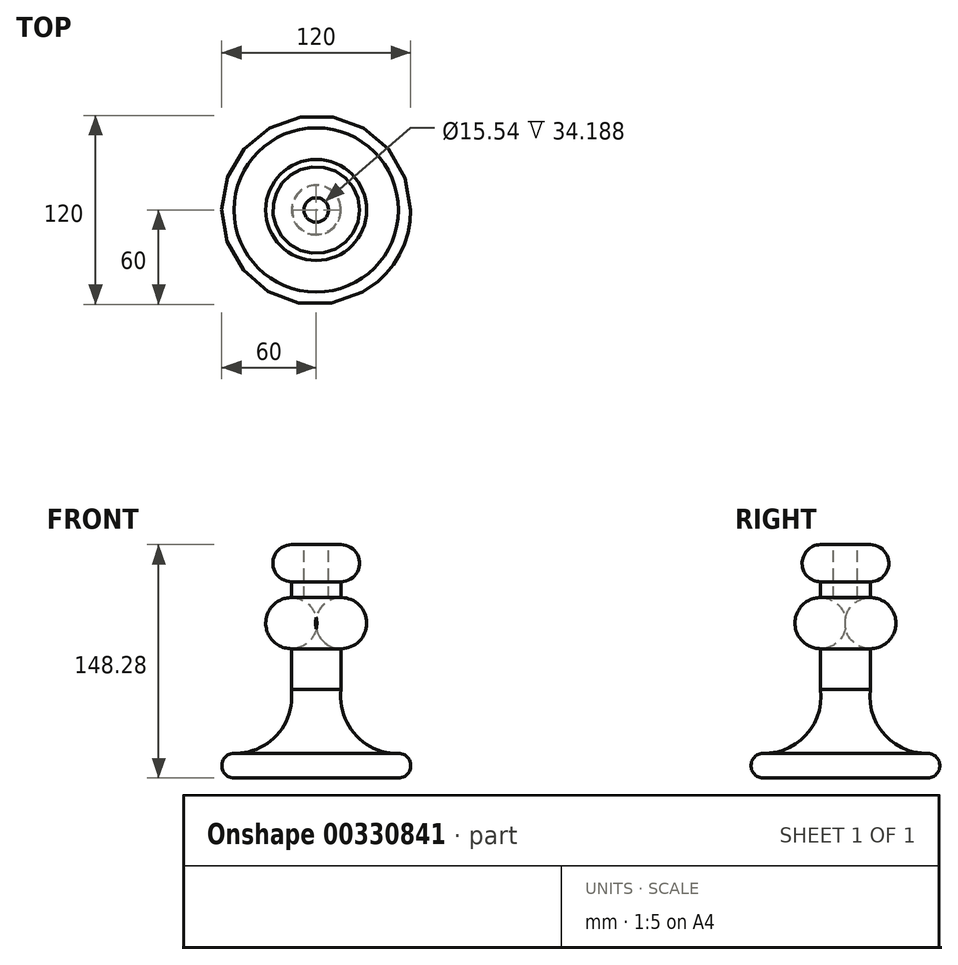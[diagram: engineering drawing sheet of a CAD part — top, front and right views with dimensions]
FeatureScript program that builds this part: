
annotation { "Feature Type Name" : "Feature", "Feature Type Description" : "" }
export const myFeature = defineFeature(function(context is Context, id is Id, definition is map)
    precondition{}
    {
        {
            var Q0;
            Q0=qCreatedBy(makeId("Front.planeOp"),FACE);
            var sketch = newSketch(context, id + "F0", { "sketchPlane" : qUnion([Q0])});
            skLineSegment(sketch, "E0", {"start": v(0, 0) * mm, "end": v(52.17, 0) * mm});
            skArc(sketch, "E1", {"start": v(52.17, 0) * mm, "mid": v(60, 7.82) * mm, "end": v(52.17, 15.64) * mm});
            skArc(sketch, "E2", {"start": v(15.83, 56.2) * mm, "mid": v(24.71, 27.6) * mm, "end": v(52.17, 15.64) * mm});
            skLineSegment(sketch, "E3", {"start": v(15.83, 56.2) * mm, "end": v(15.83, 82.12) * mm});
            skArc(sketch, "E4", {"start": v(15.83, 124.63) * mm, "mid": v(27.54, 136.42) * mm, "end": v(15.83, 148.22) * mm});
            skLineSegment(sketch, "E5", {"start": v(15.83, 148.22) * mm, "end": v(7.77, 148.28) * mm});
            skLineSegment(sketch, "E6", {"start": v(7.77, 148.28) * mm, "end": v(7.77, 114.09) * mm});
            skLineSegment(sketch, "E7", {"start": v(7.77, 114.09) * mm, "end": v(0, 114.09) * mm});
            skLineSegment(sketch, "E8", {"start": v(0, 114.09) * mm, "end": v(0, 101.9) * mm});
            skArc(sketch, "E9", {"start": v(0, 101.9) * mm, "mid": v(-0.4, 98.35) * mm, "end": v(0, 94.78) * mm});
            skArc(sketch, "E10.trimOffspring", {"start": v(15.83, 82.12) * mm, "mid": v(32.06, 98.35) * mm, "end": v(15.83, 114.58) * mm});
            skLineSegment(sketch, "E11.trimOffspring", {"start": v(15.83, 114.58) * mm, "end": v(15.83, 124.63) * mm});
            skLineSegment(sketch, "E12.trimOffspring", {"start": v(0, 94.78) * mm, "end": v(0, 0) * mm});
            skSolve(sketch);
        }
        {
            var Q0;
            Q0=makeQuery(id+"F0.imprint","IMPRINT",FACE,{"disambiguationData":[TD([[makeQuery(id+"F0.imprint","IMPRINT",EDGE,{"derivedFrom":sQuery(id+"F0.wireOp",EDGE,"E0")}),1.0]])]});
            var Q1;
            Q1=sQuery(id+"F0.wireOp",EDGE,"E12.trimOffspring");
            revolve(context, id + "F1", {"entities" : qUnion([Q0]), "axis" : qUnion([Q1]), "revolveType" : RevolveType.FULL});
        }
    });
